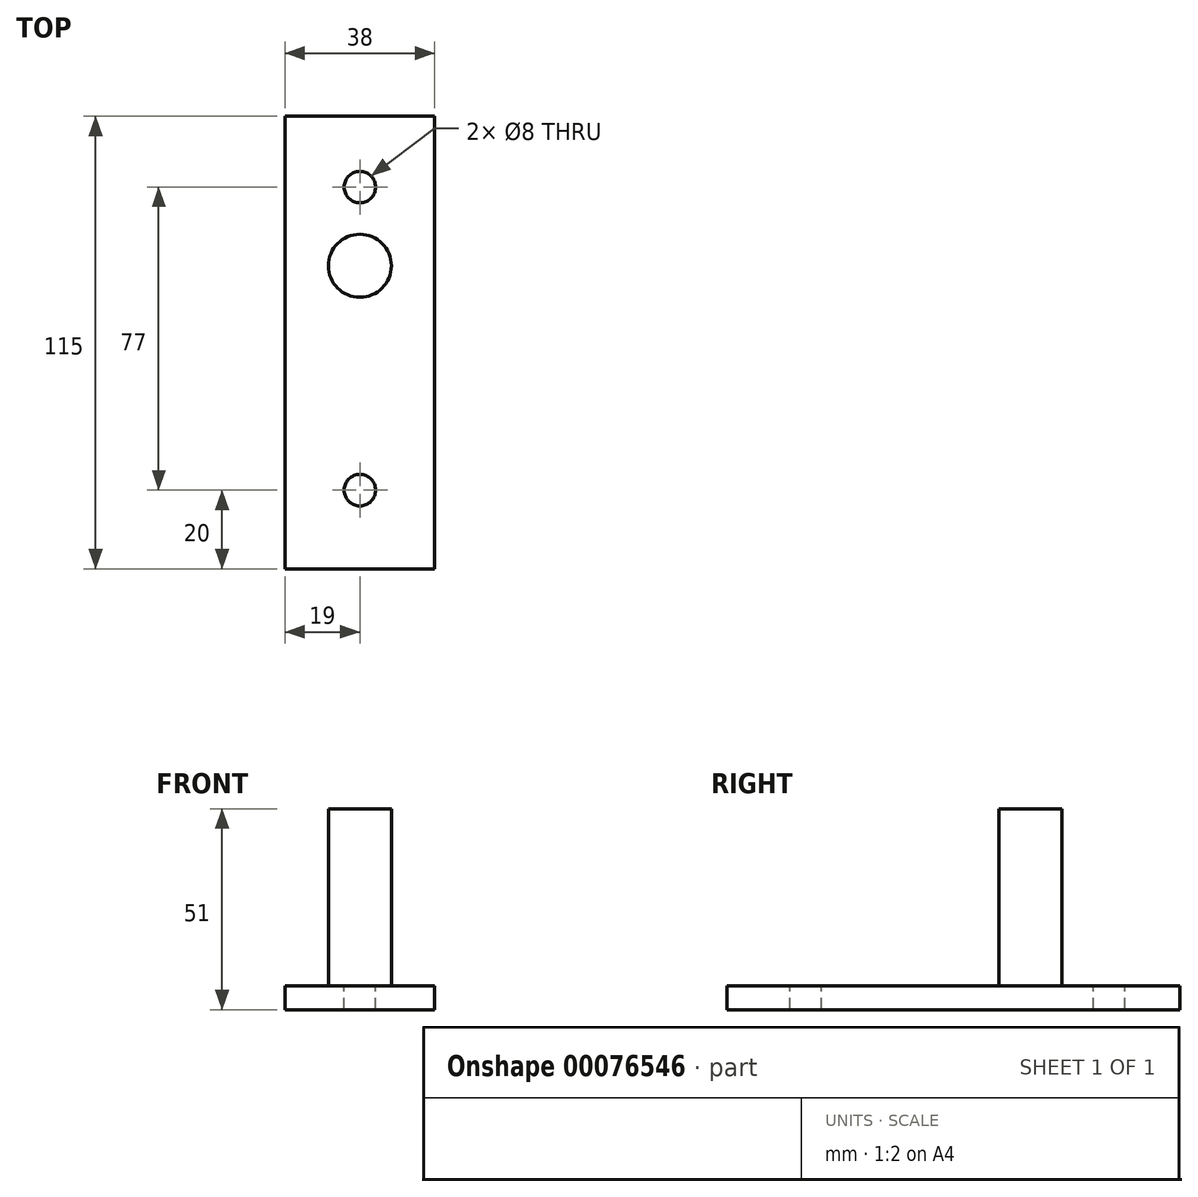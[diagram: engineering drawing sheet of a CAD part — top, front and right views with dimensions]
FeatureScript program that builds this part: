
annotation { "Feature Type Name" : "Feature", "Feature Type Description" : "" }
export const myFeature = defineFeature(function(context is Context, id is Id, definition is map)
    precondition{}
    {
        {
            var Q0;
            Q0=qCreatedBy(makeId("Top.planeOp"),FACE);
            var sketch = newSketch(context, id + "F0", { "sketchPlane" : qUnion([Q0])});
            skLineSegment(sketch, "E0", {"start": v(0, 57.5) * mm, "end": v(19, 57.5) * mm});
            skLineSegment(sketch, "E1", {"start": v(19, 57.5) * mm, "end": v(19, 0) * mm});
            skLineSegment(sketch, "E2.MirrorCS", {"start": v(19, -57.5) * mm, "end": v(19, 0) * mm});
            skLineSegment(sketch, "E3.MirrorCS", {"start": v(0, -57.5) * mm, "end": v(19, -57.5) * mm});
            skLineSegment(sketch, "E4.MirrorCS", {"start": v(0, 57.5) * mm, "end": v(-19, 57.5) * mm});
            skLineSegment(sketch, "E5.MirrorCS", {"start": v(-19, 57.5) * mm, "end": v(-19, 0) * mm});
            skLineSegment(sketch, "E6.MirrorCS", {"start": v(-19, -57.5) * mm, "end": v(-19, 0) * mm});
            skLineSegment(sketch, "E7.MirrorCS", {"start": v(0, -57.5) * mm, "end": v(-19, -57.5) * mm});
            skSolve(sketch);
        }
        {
            var Q0;
            Q0=makeQuery(id+"F0.imprint","IMPRINT",FACE,{"disambiguationData":[TD([[makeQuery(id+"F0.imprint","IMPRINT",EDGE,{"derivedFrom":sQuery(id+"F0.wireOp",EDGE,"E0")}),-1.0]])]});
            extrude(context, id + "F1", {"entities" : qUnion([Q0]), "depth" : 6 * mm});
        }
        {
            var Q0;
            Q0=makeQuery(id+"F1.opExtrude","CAP_FACE",FACE,{"disambiguationData":[OSD([sQuery(id+"F0.wireOp",EDGE,"E0"),sQuery(id+"F0.wireOp",EDGE,"E1"),sQuery(id+"F0.wireOp",EDGE,"E2.MirrorCS"),sQuery(id+"F0.wireOp",EDGE,"E3.MirrorCS"),sQuery(id+"F0.wireOp",EDGE,"E4.MirrorCS"),sQuery(id+"F0.wireOp",EDGE,"E5.MirrorCS"),sQuery(id+"F0.wireOp",EDGE,"E6.MirrorCS"),sQuery(id+"F0.wireOp",EDGE,"E7.MirrorCS")])],"isStart":false});
            var sketch = newSketch(context, id + "F2", { "sketchPlane" : qUnion([Q0])});
            skCircle(sketch, "E8", {"center": v(0, 19.5) * mm, "radius": 8 * mm});
            skSolve(sketch);
        }
        {
            var Q0;
            Q0=makeQuery(id+"F2.imprint","IMPRINT",FACE,{"disambiguationData":[TD([[makeQuery(id+"F2.imprint","IMPRINT",EDGE,{"derivedFrom":sQuery(id+"F2.wireOp",EDGE,"E8")}),-1.0]])]});
            var sketch = newSketch(context, id + "F3", { "sketchPlane" : qUnion([Q0])});
            skCircle(sketch, "E9", {"center": v(0, 39.5) * mm, "radius": 4 * mm});
            skSolve(sketch);
        }
        {
            var Q0;
            Q0=makeQuery(id+"F2.imprint","IMPRINT",FACE,{"disambiguationData":[TD([[makeQuery(id+"F2.imprint","IMPRINT",EDGE,{"derivedFrom":sQuery(id+"F2.wireOp",EDGE,"E8")}),-1.0]])]});
            var sketch = newSketch(context, id + "F4", { "sketchPlane" : qUnion([Q0])});
            skCircle(sketch, "E10", {"center": v(0, -37.5) * mm, "radius": 4 * mm});
            skSolve(sketch);
        }
        {
            var Q0;
            Q0=makeQuery(id+"F2.imprint","IMPRINT",FACE,{"disambiguationData":[TD([[makeQuery(id+"F2.imprint","IMPRINT",EDGE,{"derivedFrom":sQuery(id+"F2.wireOp",EDGE,"E8")}),1.0]])]});
            extrude(context, id + "F5", {"entities" : qUnion([Q0]), "operationType" : NewBodyOperationType.ADD, "depth" : 45 * mm});
        }
        {
            var Q0;
            Q0=makeQuery(id+"F3.imprint","IMPRINT",FACE,{"disambiguationData":[TD([[makeQuery(id+"F3.imprint","IMPRINT",EDGE,{"derivedFrom":sQuery(id+"F3.wireOp",EDGE,"E9")}),1.0]])]});
            extrude(context, id + "F6", {"entities" : qUnion([Q0]), "operationType" : NewBodyOperationType.REMOVE, "endBound" : BoundingType.THROUGH_ALL, "oppositeDirection" : true, "depth" : 25.4 * mm});
        }
        {
            var Q0;
            Q0=makeQuery(id+"F4.imprint","IMPRINT",FACE,{"disambiguationData":[TD([[makeQuery(id+"F4.imprint","IMPRINT",EDGE,{"derivedFrom":sQuery(id+"F4.wireOp",EDGE,"E10")}),1.0]])]});
            var Q1;
            Q1=sQuery(id+"F4.wireOp",EDGE,"E10");
            extrude(context, id + "F7", {"entities" : qUnion([Q0]), "operationType" : NewBodyOperationType.REMOVE, "surfaceEntities" : qUnion([Q1]), "endBound" : BoundingType.THROUGH_ALL, "oppositeDirection" : true, "depth" : 25.4 * mm});
        }
    });
